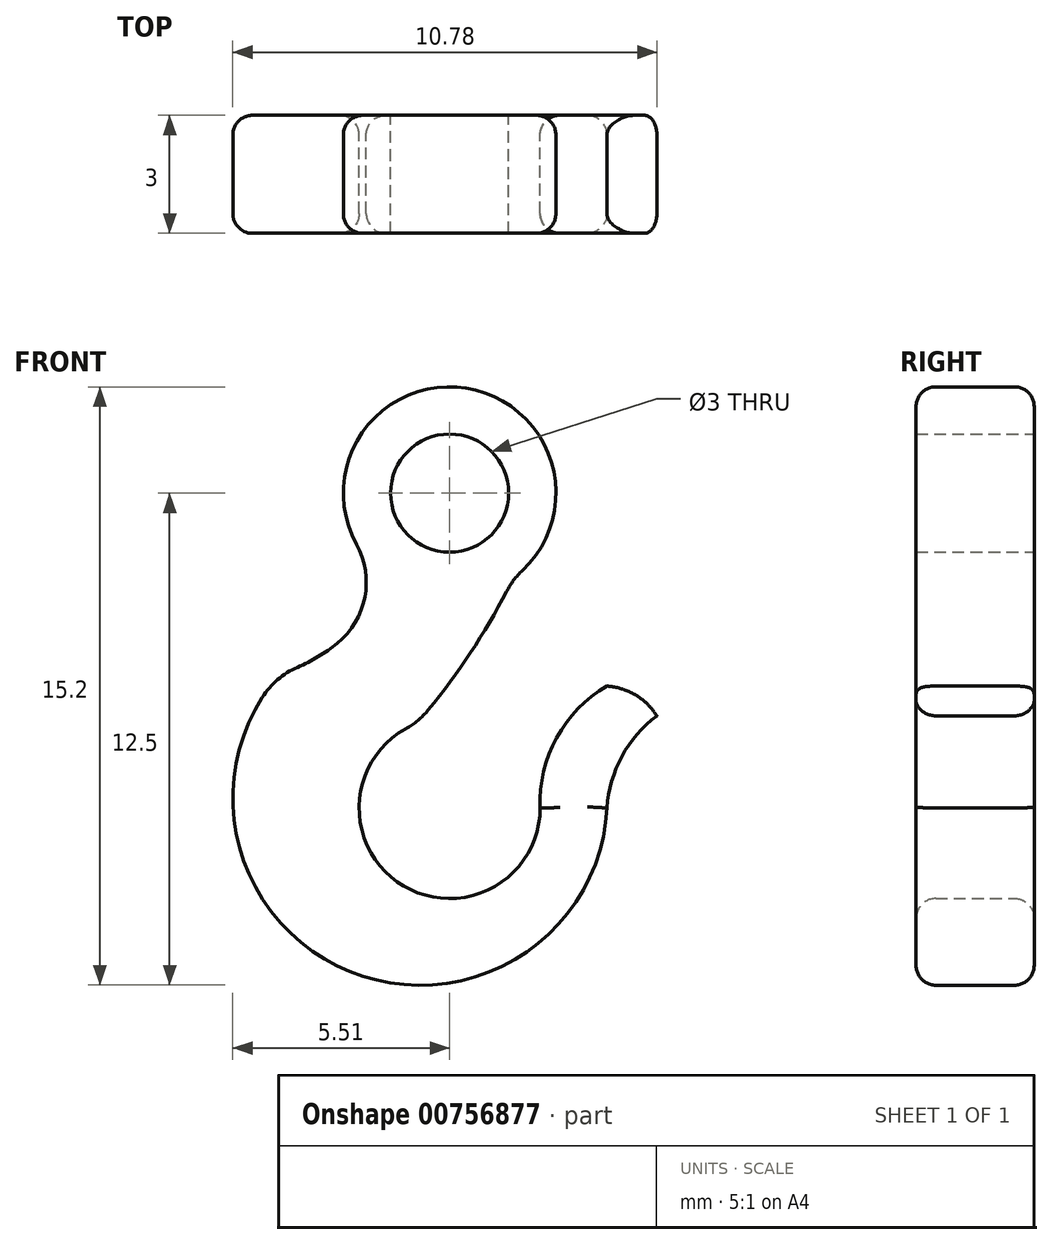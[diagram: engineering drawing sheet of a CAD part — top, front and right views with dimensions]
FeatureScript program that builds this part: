
annotation { "Feature Type Name" : "Feature", "Feature Type Description" : "" }
export const myFeature = defineFeature(function(context is Context, id is Id, definition is map)
    precondition{}
    {
        {
            var Q0;
            Q0=qCreatedBy(makeId("Front.planeOp"),FACE);
            var sketch = newSketch(context, id + "F0", { "sketchPlane" : qUnion([Q0])});
            skCircle(sketch, "E0", {"center": v(0, 0) * mm, "radius": 1.5 * mm});
            skArc(sketch, "E1", {"start": v(1.85, -1.96) * mm, "mid": v(0.42, 2.67) * mm, "end": v(-2.37, -1.3) * mm});
            skLineSegment(sketch, "E2", {"start": v(0, 0) * mm, "end": v(0, -32.33) * mm, "construction": true});
            skLineSegment(sketch, "E3", {"start": v(-5.7, -13.7) * mm, "end": v(7.57, -13.7) * mm, "construction": true});
            skLineSegment(sketch, "E4", {"start": v(-7.25, -2.7) * mm, "end": v(9.05, -2.7) * mm, "construction": true});
            skArc(sketch, "E5", {"start": v(-0.84, -5.86) * mm, "mid": v(0.42, -10.26) * mm, "end": v(0, -5.7) * mm, "construction": true});
            skLineSegment(sketch, "E6", {"start": v(1.62, -2.16) * mm, "end": v(-0.84, -5.86) * mm, "construction": true});
            skLineSegment(sketch, "E7", {"start": v(-1.62, -2.16) * mm, "end": v(-5.5, -8) * mm, "construction": true});
            skLineSegment(sketch, "E8", {"start": v(-1.62, -2.16) * mm, "end": v(1.62, -2.16) * mm, "construction": true});
            skLineSegment(sketch, "E9", {"start": v(4, -8) * mm, "end": v(-9.91, -8) * mm, "construction": true});
            skLineSegment(sketch, "E10", {"start": v(4, -4.9) * mm, "end": v(4, -12.5) * mm, "construction": true});
            skLineSegment(sketch, "E11", {"start": v(4, -12.5) * mm, "end": v(-9.63, -12.5) * mm, "construction": true});
            skLineSegment(sketch, "E12", {"start": v(2.8, -6.72) * mm, "end": v(5.48, -2.68) * mm, "construction": true});
            skArc(sketch, "E13", {"start": v(-1.12, -5.99) * mm, "mid": v(-1.12, -10) * mm, "end": v(2.3, -7.9) * mm});
            skArc(sketch, "E14", {"start": v(-0.54, -5.51) * mm, "mid": v(0.53, -4.06) * mm, "end": v(1.45, -2.5) * mm});
            skArc(sketch, "E15", {"start": v(-4.76, -5.19) * mm, "mid": v(-1.96, -12.35) * mm, "end": v(4, -7.5) * mm});
            skPoint(sketch, "E15.third.point", {"position": v(-0.57, -12.5) * mm});
            skArc(sketch, "E16", {"start": v(-3.86, -4.43) * mm, "mid": v(-3.34, -4.16) * mm, "end": v(-2.85, -3.82) * mm});
            skArc(sketch, "E17", {"start": v(5.27, -5.66) * mm, "mid": v(4.38, -6.7) * mm, "end": v(4, -8) * mm});
            skArc(sketch, "E18", {"start": v(5.27, -5.66) * mm, "mid": v(4.72, -5.13) * mm, "end": v(4, -4.9) * mm});
            skArc(sketch, "E19", {"start": v(4, -4.9) * mm, "mid": v(2.72, -6.22) * mm, "end": v(2.3, -8) * mm});
            skPoint(sketch, "E20.visualSharp", {"position": v(-1.62, -2.16) * mm});
            skArc(sketch, "E20.filletArc", {"start": v(-2.85, -3.82) * mm, "mid": v(-2.15, -2.65) * mm, "end": v(-2.37, -1.3) * mm});
            skPoint(sketch, "E21.visualSharp", {"position": v(1.62, -2.16) * mm});
            skArc(sketch, "E21.filletArc", {"start": v(1.85, -1.96) * mm, "mid": v(1.63, -2.21) * mm, "end": v(1.45, -2.5) * mm});
            skPoint(sketch, "E22.visualSharp", {"position": v(-4.3, -4.59) * mm});
            skArc(sketch, "E22.filletArc", {"start": v(-3.86, -4.43) * mm, "mid": v(-4.37, -4.74) * mm, "end": v(-4.76, -5.19) * mm});
            skPoint(sketch, "E23.visualSharp", {"position": v(-0.84, -5.86) * mm});
            skArc(sketch, "E23.filletArc", {"start": v(-1.12, -5.99) * mm, "mid": v(-0.8, -5.78) * mm, "end": v(-0.54, -5.51) * mm});
            skSolve(sketch);
        }
        {
            var Q0;
            Q0 = qSketchRegion(id + "F0", true);
            extrude(context, id + "F1", {"entities" : qUnion([Q0]), "depth" : 3 * mm, "offsetDistance" : 25 * mm});
        }
        {
            var Q0;
            Q0=makeQuery(id+"F1.opExtrude","CAP_EDGE",EDGE,{"disambiguationData":[OSD([sQuery(id+"F0.wireOp",EDGE,"E14")])],"isStart":false});
            var Q1;
            Q1=makeQuery(id+"F1.opExtrude","CAP_EDGE",EDGE,{"disambiguationData":[OSD([sQuery(id+"F0.wireOp",EDGE,"E14")])],"isStart":true});
            var Q2;
            Q2=makeQuery(id+"F1.opExtrude","CAP_EDGE",EDGE,{"disambiguationData":[OSD([sQuery(id+"F0.wireOp",EDGE,"E19")])],"isStart":true});
            var Q3;
            Q3=makeQuery(id+"F1.opExtrude","CAP_EDGE",EDGE,{"disambiguationData":[OSD([sQuery(id+"F0.wireOp",EDGE,"E19")])],"isStart":false});
            fillet(context, id + "F2", {"entities" : qUnion([Q0, Q1, Q2, Q3]), "radius" : 0.5 * mm, "tangentPropagation" : true, "allowEdgeOverflow" : false});
        }
    });
